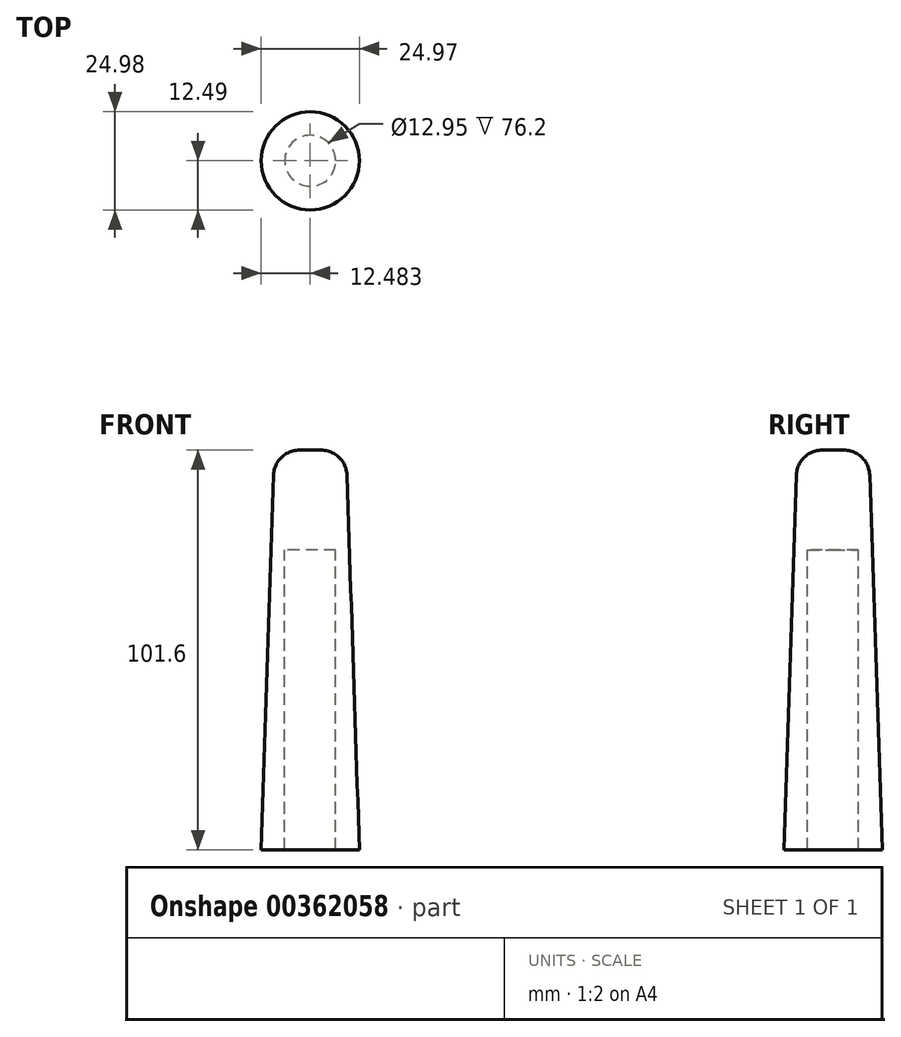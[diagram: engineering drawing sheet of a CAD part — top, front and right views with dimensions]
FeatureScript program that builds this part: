
annotation { "Feature Type Name" : "Feature", "Feature Type Description" : "" }
export const myFeature = defineFeature(function(context is Context, id is Id, definition is map)
    precondition{}
    {
        {
            var Q0;
            Q0=qCreatedBy(makeId("Front.planeOp"),FACE);
            var sketch = newSketch(context, id + "F0", { "sketchPlane" : qUnion([Q0])});
            skLineSegment(sketch, "E0", {"start": v(0, 0) * mm, "end": v(5.08, 0) * mm});
            skLineSegment(sketch, "E1", {"start": v(5.08, 0) * mm, "end": v(2.84, 67.28) * mm});
            skLineSegment(sketch, "E2", {"start": v(-3.76, 73.66) * mm, "end": v(-6.48, 73.66) * mm});
            skLineSegment(sketch, "E3", {"start": v(-6.48, 73.66) * mm, "end": v(-6.48, 48.26) * mm});
            skLineSegment(sketch, "E4", {"start": v(-6.48, 48.26) * mm, "end": v(0, 48.26) * mm});
            skLineSegment(sketch, "E5", {"start": v(0, 48.26) * mm, "end": v(0, 0) * mm});
            skPoint(sketch, "E6.visualSharp", {"position": v(2.63, 73.66) * mm});
            skArc(sketch, "E6.filletArc", {"start": v(2.84, 67.28) * mm, "mid": v(0.84, 71.8) * mm, "end": v(-3.76, 73.66) * mm});
            skLineSegment(sketch, "E7", {"start": v(0, 0) * mm, "end": v(0, -27.94) * mm});
            skLineSegment(sketch, "E8", {"start": v(0, -27.94) * mm, "end": v(6, -27.94) * mm});
            skLineSegment(sketch, "E9", {"start": v(6, -27.94) * mm, "end": v(5.08, 0) * mm});
            skSolve(sketch);
        }
        {
            var Q0;
            Q0 = qSketchRegion(id + "F0", true);
            var Q1;
            Q1=sQuery(id+"F0.wireOp",EDGE,"E3");
            revolve(context, id + "F1", {"entities" : qUnion([Q0]), "axis" : qUnion([Q1]), "revolveType" : RevolveType.FULL});
        }
    });
